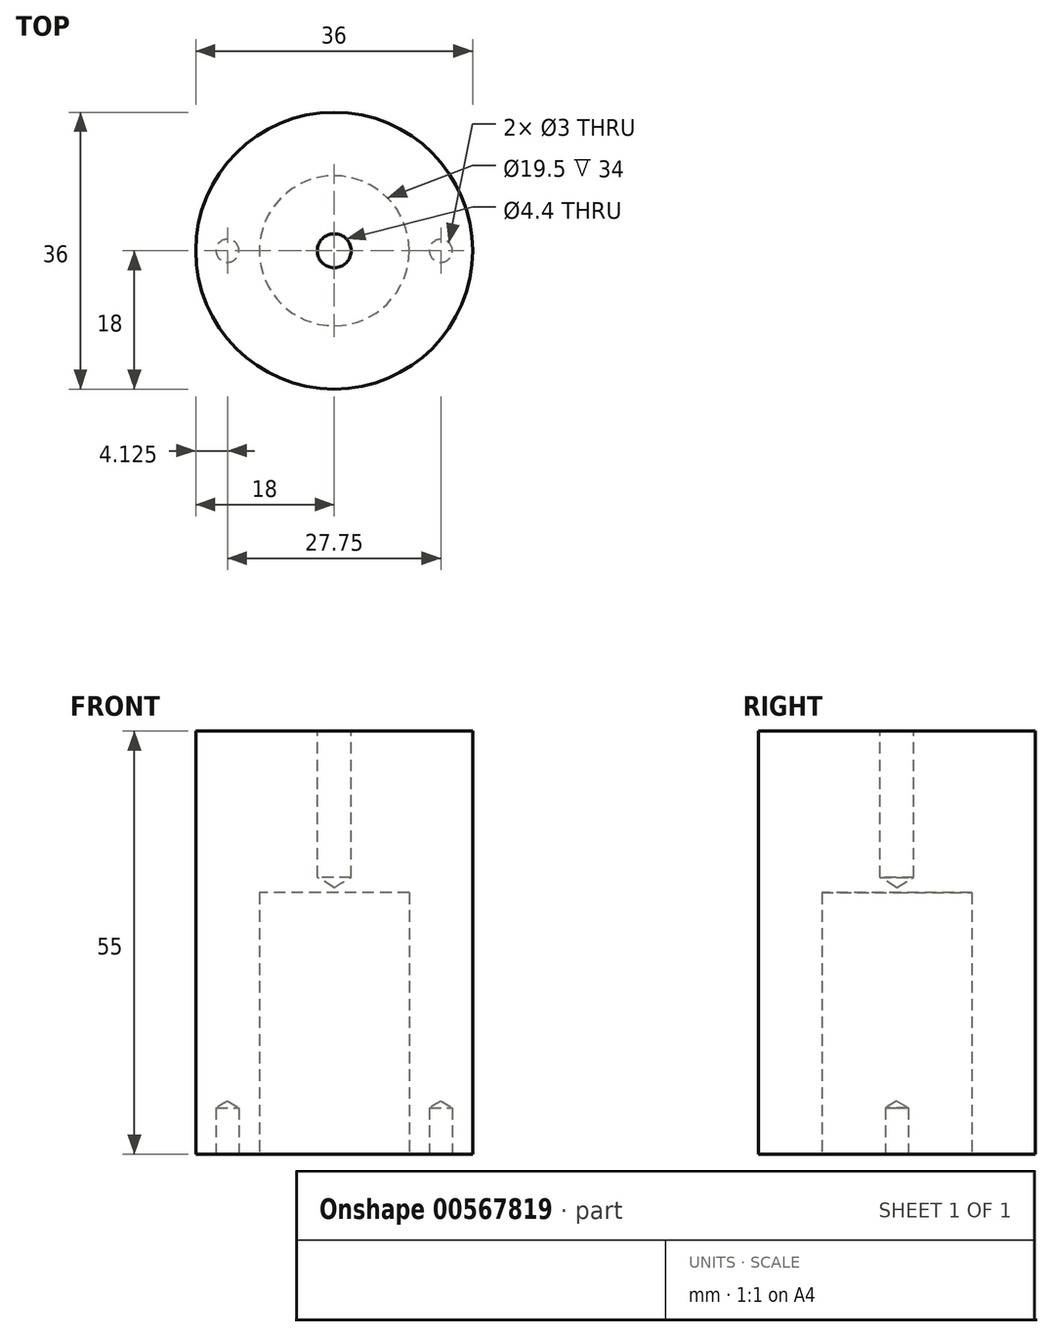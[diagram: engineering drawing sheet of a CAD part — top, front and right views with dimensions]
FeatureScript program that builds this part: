
annotation { "Feature Type Name" : "Feature", "Feature Type Description" : "" }
export const myFeature = defineFeature(function(context is Context, id is Id, definition is map)
    precondition{}
    {
        {
            var Q0;
            Q0=qCreatedBy(makeId("Top.planeOp"),FACE);
            var sketch = newSketch(context, id + "F0", { "sketchPlane" : qUnion([Q0])});
            skCircle(sketch, "E0", {"center": v(0, 0) * mm, "radius": 18 * mm});
            skCircle(sketch, "E1", {"center": v(0, 0) * mm, "radius": 9.75 * mm});
            skLineSegment(sketch, "E2", {"start": v(-18, 0) * mm, "end": v(-9.75, 0) * mm});
            skLineSegment(sketch, "E3", {"start": v(9.75, 0) * mm, "end": v(18, 0) * mm});
            skPoint(sketch, "E4", {"position": v(-13.88, 0) * mm});
            skPoint(sketch, "E5", {"position": v(13.88, 0) * mm});
            skSolve(sketch);
        }
        {
            var Q0;
            {var subQ0=sQuery(id+"F0.wireOp",EDGE,"E2");Q0=makeQuery(id+"F0.imprint","IMPRINT",FACE,{"disambiguationData":[TD([[makeQuery(id+"F0.imprint","IMPRINT",EDGE,{"derivedFrom":subQ0}),1.0]])]});}
            var Q1;
            {var subQ0=sQuery(id+"F0.wireOp",EDGE,"E2");Q1=makeQuery(id+"F0.imprint","IMPRINT",FACE,{"disambiguationData":[TD([[makeQuery(id+"F0.imprint","IMPRINT",EDGE,{"derivedFrom":subQ0}),-1.0]])]});}
            extrude(context, id + "F1", {"entities" : qUnion([Q0, Q1]), "depth" : 4 * mm, "offsetDistance" : 25 * mm});
        }
        {
            var Q0;
            Q0=makeQuery(id+"F0.imprint","IMPRINT",FACE,{"disambiguationData":[TD([[makeQuery(id+"F0.imprint","IMPRINT",EDGE,{"derivedFrom":sQuery(id+"F0.wireOp",EDGE,"E0")}),1.0]])]});
            extrude(context, id + "F2", {"entities" : qUnion([Q0]), "operationType" : NewBodyOperationType.ADD, "depth" : 34 * mm, "offsetDistance" : 25 * mm});
        }
        {
            var Q0;
            Q0=makeQuery(id+"F2.opExtrude","CAP_FACE",FACE,{"disambiguationData":[OSD([sQuery(id+"F0.wireOp",EDGE,"E0"),sQuery(id+"F0.wireOp",EDGE,"E1")])],"isStart":false});
            var sketch = newSketch(context, id + "F3", { "sketchPlane" : qUnion([Q0])});
            skCircle(sketch, "E6", {"center": v(0, 0) * mm, "radius": 18 * mm});
            skSolve(sketch);
        }
        {
            var Q0;
            Q0 = qSketchRegion(id + "F3", true);
            extrude(context, id + "F4", {"entities" : qUnion([Q0]), "operationType" : NewBodyOperationType.ADD, "depth" : 21 * mm, "offsetDistance" : 25 * mm});
        }
        {
            var Q0;
            Q0=makeQuery(id+"F4.opExtrude","CAP_FACE",FACE,{"disambiguationData":[OSD([sQuery(id+"F3.wireOp",EDGE,"E6")])],"isStart":false});
            var sketch = newSketch(context, id + "F5", { "sketchPlane" : qUnion([Q0])});
            skPoint(sketch, "E7", {"position": v(0, 0) * mm});
            skSolve(sketch);
        }
        {
            var Q0;
            Q0=sQuery(id+"F5.wireOp",VERTEX,"E7");
            var Q1;
            Q1=makeQuery(id+"F1.opExtrude","SWEPT_BODY",BODY,{"disambiguationData":[OSD([sQuery(id+"F0.wireOp",EDGE,"E0")])]});
            hole(context, id + "F6", {"style" : HoleStyle.SIMPLE, "endStyle" : HoleEndStyle.BLIND, "standardTappedOrClearance" : lookupTablePath({ "standard" : "ISO", "fit" : "Normal", "size" : "M4", "type" : "Clearance" }), "standardBlindInLast" : lookupTablePath({ "fit" : "Standard", "standard" : "ISO", "size" : "M4", "type" : "Clearance" }), "holeDiameter" : 4.4 * mm, "majorDiameter" : 5 * mm, "holeDepth" : 19 * mm, "isTappedThrough" : true, "tappedDepth" : 12 * mm, "tapClearance" : 3, "locations" : qUnion([Q0]), "scope" : qUnion([Q1])});
        }
        {
            var Q0;
            Q0=sQuery(id+"F0.wireOp",VERTEX,"E5");
            var Q1;
            Q1=sQuery(id+"F0.wireOp",VERTEX,"E4");
            var Q2;
            Q2=makeQuery(id+"F1.opExtrude","SWEPT_BODY",BODY,{"disambiguationData":[OSD([sQuery(id+"F0.wireOp",EDGE,"E0"),sQuery(id+"F0.wireOp",EDGE,"E1")])]});
            hole(context, id + "F7", {"style" : HoleStyle.SIMPLE, "endStyle" : HoleEndStyle.BLIND, "oppositeDirection" : true, "holeDiameter" : 3 * mm, "majorDiameter" : 5 * mm, "holeDepth" : 6 * mm, "isTappedThrough" : true, "tappedDepth" : 12 * mm, "tapClearance" : 3, "locations" : qUnion([Q0, Q1]), "scope" : qUnion([Q2])});
        }
    });
